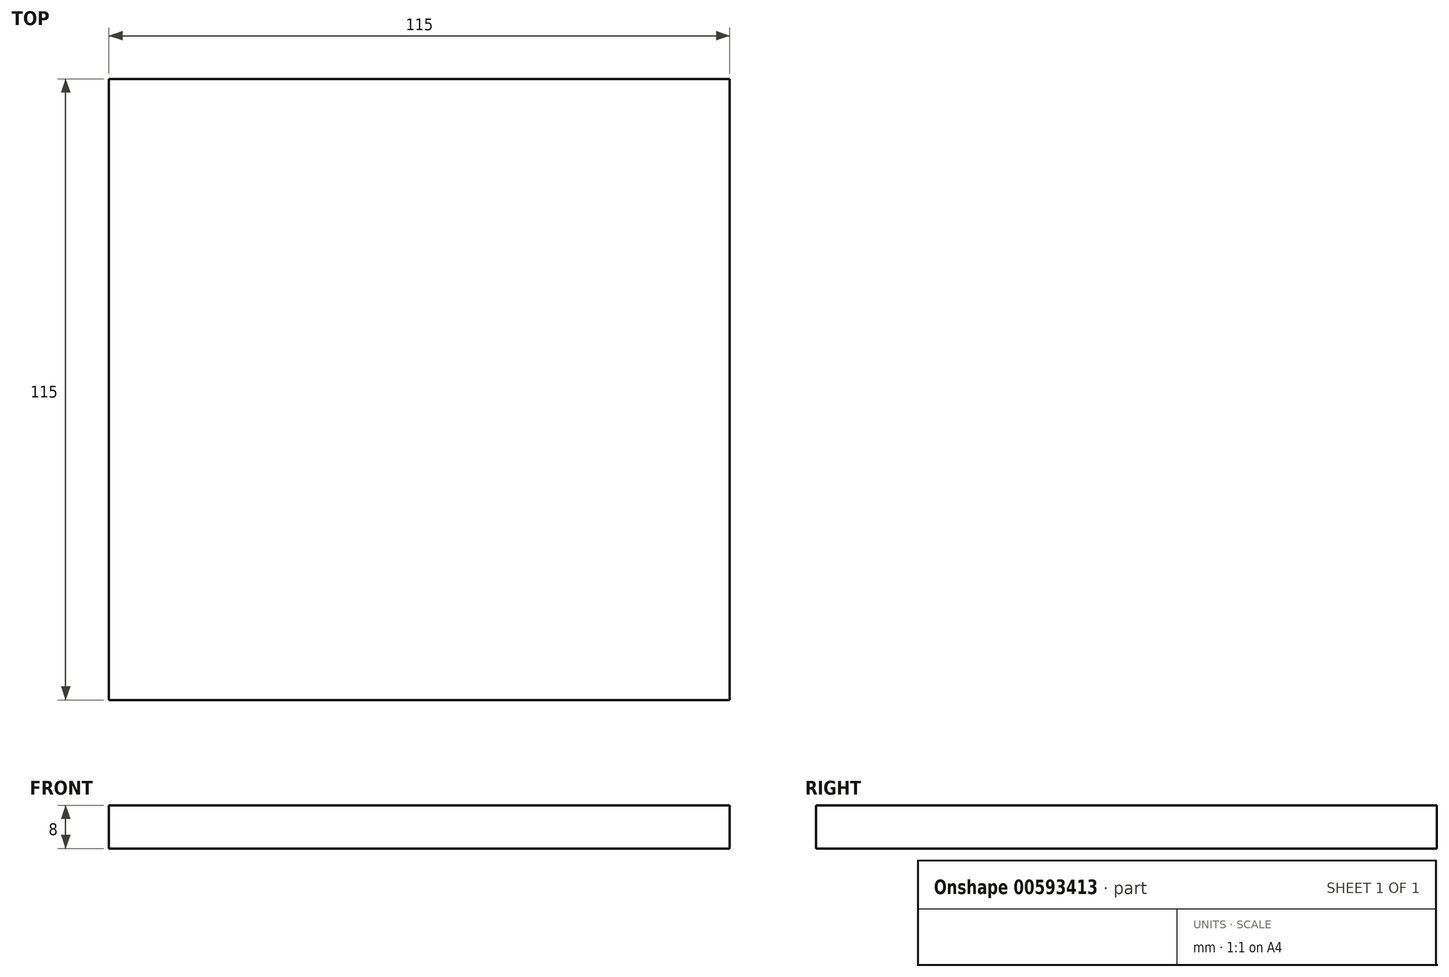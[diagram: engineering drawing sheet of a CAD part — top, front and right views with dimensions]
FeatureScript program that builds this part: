
annotation { "Feature Type Name" : "Feature", "Feature Type Description" : "" }
export const myFeature = defineFeature(function(context is Context, id is Id, definition is map)
    precondition{}
    {
        {
            var Q0;
            Q0=qCreatedBy(makeId("Top.planeOp"),FACE);
            var sketch = newSketch(context, id + "F0", { "sketchPlane" : qUnion([Q0])});
            skLineSegment(sketch, "E0.bottom", {"start": v(-57.5, 57.5) * mm, "end": v(57.5, 57.5) * mm});
            skLineSegment(sketch, "E0.top", {"start": v(-57.5, -57.5) * mm, "end": v(57.5, -57.5) * mm});
            skLineSegment(sketch, "E0.left", {"start": v(-57.5, 57.5) * mm, "end": v(-57.5, -57.5) * mm});
            skLineSegment(sketch, "E0.right", {"start": v(57.5, 57.5) * mm, "end": v(57.5, -57.5) * mm});
            skPoint(sketch, "E0.middle", {"position": v(0, 0) * mm});
            skSolve(sketch);
        }
        {
            var Q0;
            Q0 = qSketchRegion(id + "F0", true);
            extrude(context, id + "F1", {"entities" : qUnion([Q0]), "depth" : 8 * mm, "offsetDistance" : 25 * mm});
        }
    });
